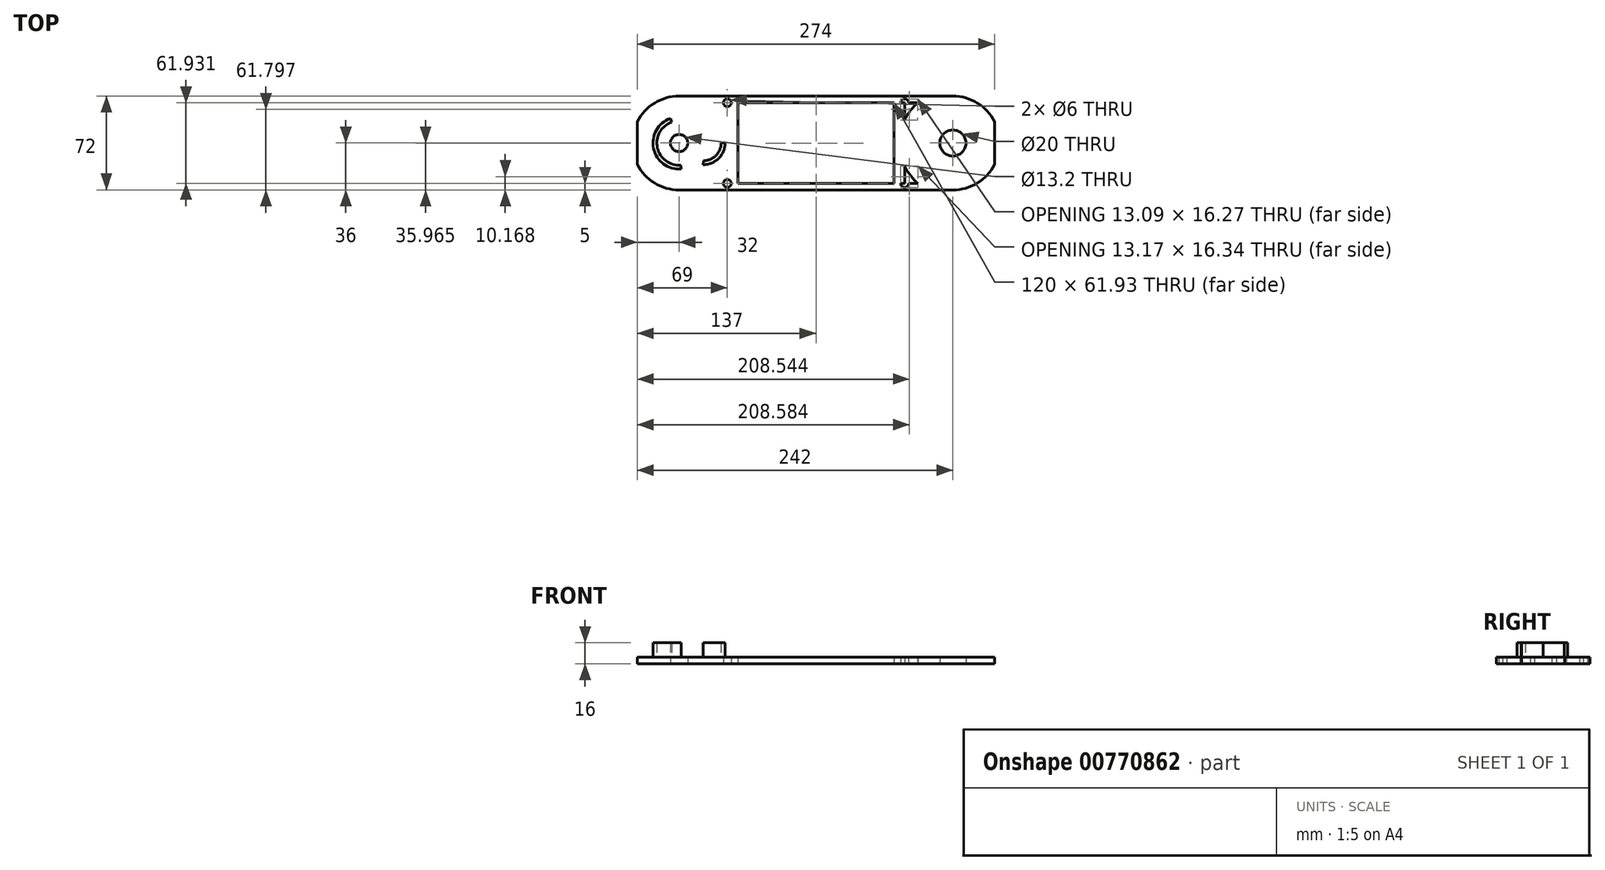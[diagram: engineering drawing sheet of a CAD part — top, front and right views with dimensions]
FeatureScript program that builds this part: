
annotation { "Feature Type Name" : "Feature", "Feature Type Description" : "" }
export const myFeature = defineFeature(function(context is Context, id is Id, definition is map)
    precondition{}
    {
        {
            var Q0;
            Q0=qCreatedBy(makeId("Top.planeOp"),FACE);
            var sketch = newSketch(context, id + "F0", { "sketchPlane" : qUnion([Q0])});
            skCircle(sketch, "E0", {"center": v(0, 0) * mm, "radius": 36 * mm});
            skCircle(sketch, "E1", {"center": v(210, 0) * mm, "radius": 36 * mm});
            skLineSegment(sketch, "E2", {"start": v(0, 36) * mm, "end": v(210, 36) * mm});
            skLineSegment(sketch, "E3", {"start": v(210, -36) * mm, "end": v(0, -36) * mm});
            skCircle(sketch, "E4", {"center": v(0, 0) * mm, "radius": 6.6 * mm});
            skCircle(sketch, "E5", {"center": v(0, 0) * mm, "radius": 10 * mm});
            skCircle(sketch, "E6", {"center": v(0, 0) * mm, "radius": 30 * mm});
            skCircle(sketch, "E7", {"center": v(210, 0) * mm, "radius": 30 * mm});
            skCircle(sketch, "E8", {"center": v(210, 0) * mm, "radius": 10 * mm});
            skCircle(sketch, "E9", {"center": v(210, 0) * mm, "radius": 14 * mm});
            skLineSegment(sketch, "E10", {"start": v(18.42, 30.93) * mm, "end": v(191.58, 30.93) * mm});
            skLineSegment(sketch, "E11", {"start": v(18.3, -31) * mm, "end": v(191.7, -31) * mm});
            skLineSegment(sketch, "E12", {"start": v(165, 30.93) * mm, "end": v(165, -31) * mm});
            skLineSegment(sketch, "E13", {"start": v(45, 30.93) * mm, "end": v(45, -31) * mm});
            skCircle(sketch, "E14", {"center": v(210, 0) * mm, "radius": 41 * mm});
            skCircle(sketch, "E15", {"center": v(0, 0) * mm, "radius": 41 * mm});
            skLineSegment(sketch, "E16.bottom", {"start": v(37, 30.93) * mm, "end": v(173, 30.93) * mm});
            skLineSegment(sketch, "E16.top", {"start": v(37, -31) * mm, "end": v(173, -31) * mm});
            skLineSegment(sketch, "E16.left", {"start": v(37, 30.93) * mm, "end": v(37, -31) * mm});
            skLineSegment(sketch, "E16.right", {"start": v(173, 30.93) * mm, "end": v(173, -31) * mm});
            skCircle(sketch, "E17", {"center": v(37, 30.93) * mm, "radius": 3 * mm});
            skCircle(sketch, "E18", {"center": v(37, -31) * mm, "radius": 3 * mm});
            skCircle(sketch, "E19", {"center": v(173, 30.93) * mm, "radius": 3 * mm});
            skCircle(sketch, "E20", {"center": v(173, -31) * mm, "radius": 3 * mm});
            skLineSegment(sketch, "E21", {"start": v(-32, -16.5) * mm, "end": v(-32, 16.5) * mm});
            skLineSegment(sketch, "E22", {"start": v(242, -16.5) * mm, "end": v(242, 16.5) * mm});
            skSolve(sketch);
        }
        {
            var Q0;
            {var subQ0=sQuery(id+"F0.wireOp",EDGE,"E16.left");var subQ1=sQuery(id+"F0.wireOp",EDGE,"E15");var subQ2=makeQuery(id+"F0.imprint","INTERSECT",VERTEX,{"disambiguationData":[OD(0.0)],"derivedFrom":[subQ1,subQ0]});Q0=makeQuery(id+"F0.imprint","IMPRINT",FACE,{"disambiguationData":[TD([[makeQuery(id+"F0.imprint","IMPRINT",EDGE,{"disambiguationData":[TD([[subQ2,1.0]])],"derivedFrom":subQ1}),1.0]])]});}
            var Q1;
            Q1=makeQuery(id+"F0.imprint","IMPRINT",FACE,{"disambiguationData":[TD([[makeQuery(id+"F0.imprint","IMPRINT",EDGE,{"derivedFrom":sQuery(id+"F0.wireOp",EDGE,"E4")}),-1.0]])]});
            var Q2;
            {var subQ0=sQuery(id+"F0.wireOp",EDGE,"E2");var subQ1=sQuery(id+"F0.wireOp",EDGE,"E1");var subQ2=makeQuery(id+"F0.imprint","INTERSECT",VERTEX,{"derivedFrom":[subQ1,subQ0]});Q2=makeQuery(id+"F0.imprint","IMPRINT",FACE,{"disambiguationData":[TD([[makeQuery(id+"F0.imprint","IMPRINT",EDGE,{"disambiguationData":[TD([[subQ2,-1.0]])],"derivedFrom":subQ1}),-1.0]])]});}
            var Q3;
            Q3=makeQuery(id+"F0.imprint","IMPRINT",FACE,{"disambiguationData":[TD([[makeQuery(id+"F0.imprint","IMPRINT",EDGE,{"derivedFrom":sQuery(id+"F0.wireOp",EDGE,"E5")}),-1.0]])]});
            var Q4;
            Q4=makeQuery(id+"F0.imprint","IMPRINT",FACE,{"disambiguationData":[TD([[makeQuery(id+"F0.imprint","IMPRINT",EDGE,{"derivedFrom":sQuery(id+"F0.wireOp",EDGE,"E8")}),-1.0]])]});
            var Q5;
            {var subQ0=sQuery(id+"F0.wireOp",EDGE,"E3");var subQ1=sQuery(id+"F0.wireOp",EDGE,"E0");var subQ2=makeQuery(id+"F0.imprint","INTERSECT",VERTEX,{"derivedFrom":[subQ1,subQ0]});Q5=makeQuery(id+"F0.imprint","IMPRINT",FACE,{"disambiguationData":[TD([[makeQuery(id+"F0.imprint","IMPRINT",EDGE,{"disambiguationData":[TD([[subQ2,-1.0]])],"derivedFrom":subQ1}),-1.0]])]});}
            var Q6;
            Q6=makeQuery(id+"F0.imprint","IMPRINT",FACE,{"disambiguationData":[TD([[makeQuery(id+"F0.imprint","IMPRINT",EDGE,{"derivedFrom":sQuery(id+"F0.wireOp",EDGE,"E7")}),-1.0]])]});
            var Q7;
            Q7=makeQuery(id+"F0.imprint","IMPRINT",FACE,{"disambiguationData":[TD([[makeQuery(id+"F0.imprint","IMPRINT",EDGE,{"derivedFrom":sQuery(id+"F0.wireOp",EDGE,"E7")}),1.0]])]});
            var Q8;
            Q8=makeQuery(id+"F0.imprint","IMPRINT",FACE,{"disambiguationData":[TD([[makeQuery(id+"F0.imprint","IMPRINT",EDGE,{"derivedFrom":sQuery(id+"F0.wireOp",EDGE,"E6")}),-1.0]])]});
            var Q9;
            {var subQ1=sQuery(id+"F0.wireOp",EDGE,"E10");var subQ5=sQuery(id+"F0.wireOp",EDGE,"E0");var subQ6=makeQuery(id+"F0.imprint","INTERSECT",VERTEX,{"derivedFrom":[subQ5,subQ1]});Q9=makeQuery(id+"F0.imprint","IMPRINT",FACE,{"disambiguationData":[TD([[makeQuery(id+"F0.imprint","IMPRINT",EDGE,{"disambiguationData":[TD([[subQ6,1.0]])],"derivedFrom":subQ5}),-1.0]])]});}
            var Q10;
            {var subQ1=sQuery(id+"F0.wireOp",EDGE,"E12");Q10=makeQuery(id+"F0.imprint","IMPRINT",FACE,{"disambiguationData":[TD([[makeQuery(id+"F0.imprint","IMPRINT",EDGE,{"derivedFrom":subQ1}),1.0]])]});}
            var Q11;
            {var subQ1=sQuery(id+"F0.wireOp",EDGE,"E1");var subQ5=sQuery(id+"F0.wireOp",EDGE,"E10");var subQ9=makeQuery(id+"F0.imprint","INTERSECT",VERTEX,{"derivedFrom":[subQ1,subQ5]});Q11=makeQuery(id+"F0.imprint","IMPRINT",FACE,{"disambiguationData":[TD([[makeQuery(id+"F0.imprint","IMPRINT",EDGE,{"disambiguationData":[TD([[subQ9,-1.0]])],"derivedFrom":subQ1}),-1.0]])]});}
            var Q12;
            {var subQ0=sQuery(id+"F0.wireOp",EDGE,"E19");var subQ1=sQuery(id+"F0.wireOp",EDGE,"E10");var subQ2=makeQuery(id+"F0.imprint","INTERSECT",VERTEX,{"derivedFrom":[subQ1,subQ0]});Q12=makeQuery(id+"F0.imprint","IMPRINT",FACE,{"disambiguationData":[TD([[makeQuery(id+"F0.imprint","IMPRINT",EDGE,{"disambiguationData":[TD([[subQ2,-1.0]])],"derivedFrom":subQ1}),-1.0]])]});}
            var Q13;
            {var subQ1=sQuery(id+"F0.wireOp",EDGE,"E13");Q13=makeQuery(id+"F0.imprint","IMPRINT",FACE,{"disambiguationData":[TD([[makeQuery(id+"F0.imprint","IMPRINT",EDGE,{"derivedFrom":subQ1}),-1.0]])]});}
            var Q14;
            {var subQ0=sQuery(id+"F0.wireOp",EDGE,"E2");var subQ1=sQuery(id+"F0.wireOp",EDGE,"E0");var subQ2=makeQuery(id+"F0.imprint","INTERSECT",VERTEX,{"derivedFrom":[subQ1,subQ0]});Q14=makeQuery(id+"F0.imprint","IMPRINT",FACE,{"disambiguationData":[TD([[makeQuery(id+"F0.imprint","IMPRINT",EDGE,{"disambiguationData":[TD([[subQ2,1.0]])],"derivedFrom":subQ1}),-1.0]])]});}
            var Q15;
            {var subQ0=sQuery(id+"F0.wireOp",EDGE,"E20");var subQ1=sQuery(id+"F0.wireOp",EDGE,"E11");var subQ2=makeQuery(id+"F0.imprint","INTERSECT",VERTEX,{"derivedFrom":[subQ1,subQ0]});Q15=makeQuery(id+"F0.imprint","IMPRINT",FACE,{"disambiguationData":[TD([[makeQuery(id+"F0.imprint","IMPRINT",EDGE,{"disambiguationData":[TD([[subQ2,-1.0]])],"derivedFrom":subQ1}),1.0]])]});}
            var Q16;
            {var subQ0=sQuery(id+"F0.wireOp",EDGE,"E15");var subQ1=sQuery(id+"F0.wireOp",EDGE,"E10");var subQ2=makeQuery(id+"F0.imprint","INTERSECT",VERTEX,{"derivedFrom":[subQ1,subQ0]});Q16=makeQuery(id+"F0.imprint","IMPRINT",FACE,{"disambiguationData":[TD([[makeQuery(id+"F0.imprint","IMPRINT",EDGE,{"disambiguationData":[TD([[subQ2,-1.0]])],"derivedFrom":subQ1}),-1.0]])]});}
            var Q17;
            {var subQ0=sQuery(id+"F0.wireOp",EDGE,"E14");var subQ1=sQuery(id+"F0.wireOp",EDGE,"E3");var subQ2=makeQuery(id+"F0.imprint","INTERSECT",VERTEX,{"derivedFrom":[subQ1,subQ0]});Q17=makeQuery(id+"F0.imprint","IMPRINT",FACE,{"disambiguationData":[TD([[makeQuery(id+"F0.imprint","IMPRINT",EDGE,{"disambiguationData":[TD([[subQ2,-1.0]])],"derivedFrom":subQ1}),-1.0]])]});}
            var Q18;
            {var subQ0=sQuery(id+"F0.wireOp",EDGE,"E15");var subQ6=sQuery(id+"F0.wireOp",EDGE,"E2");var subQ11=makeQuery(id+"F0.imprint","INTERSECT",VERTEX,{"derivedFrom":[subQ6,subQ0]});Q18=makeQuery(id+"F0.imprint","IMPRINT",FACE,{"disambiguationData":[TD([[makeQuery(id+"F0.imprint","IMPRINT",EDGE,{"disambiguationData":[TD([[subQ11,-1.0]])],"derivedFrom":subQ6}),-1.0]])]});}
            var Q19;
            {var subQ0=sQuery(id+"F0.wireOp",EDGE,"E16.right");var subQ1=sQuery(id+"F0.wireOp",EDGE,"E14");var subQ2=makeQuery(id+"F0.imprint","INTERSECT",VERTEX,{"disambiguationData":[OD(0.0)],"derivedFrom":[subQ1,subQ0]});Q19=makeQuery(id+"F0.imprint","IMPRINT",FACE,{"disambiguationData":[TD([[makeQuery(id+"F0.imprint","IMPRINT",EDGE,{"disambiguationData":[TD([[subQ2,-1.0]])],"derivedFrom":subQ1}),1.0]])]});}
            var Q20;
            {var subQ0=sQuery(id+"F0.wireOp",EDGE,"E15");var subQ1=sQuery(id+"F0.wireOp",EDGE,"E11");var subQ2=makeQuery(id+"F0.imprint","INTERSECT",VERTEX,{"derivedFrom":[subQ1,subQ0]});Q20=makeQuery(id+"F0.imprint","IMPRINT",FACE,{"disambiguationData":[TD([[makeQuery(id+"F0.imprint","IMPRINT",EDGE,{"disambiguationData":[TD([[subQ2,-1.0]])],"derivedFrom":subQ1}),1.0]])]});}
            var Q21;
            {var subQ0=sQuery(id+"F0.wireOp",EDGE,"E3");var subQ1=sQuery(id+"F0.wireOp",EDGE,"E1");var subQ2=makeQuery(id+"F0.imprint","INTERSECT",VERTEX,{"derivedFrom":[subQ1,subQ0]});Q21=makeQuery(id+"F0.imprint","IMPRINT",FACE,{"disambiguationData":[TD([[makeQuery(id+"F0.imprint","IMPRINT",EDGE,{"disambiguationData":[TD([[subQ2,1.0]])],"derivedFrom":subQ1}),-1.0]])]});}
            extrude(context, id + "F1", {"entities" : qUnion([Q0, Q1, Q2, Q3, Q4, Q5, Q6, Q7, Q8, Q9, Q10, Q11, Q12, Q13, Q14, Q15, Q16, Q17, Q18, Q19, Q20, Q21]), "depth" : 5 * mm, "offsetDistance" : 25 * mm});
        }
        {
            var Q0;
            Q0=makeQuery(id+"F1.opExtrude","CAP_FACE",FACE,{"disambiguationData":[OSD([sQuery(id+"F0.wireOp",EDGE,"E0"),sQuery(id+"F0.wireOp",EDGE,"E1"),sQuery(id+"F0.wireOp",EDGE,"E2"),sQuery(id+"F0.wireOp",EDGE,"E3"),sQuery(id+"F0.wireOp",EDGE,"E4"),sQuery(id+"F0.wireOp",EDGE,"E8"),sQuery(id+"F0.wireOp",EDGE,"E12"),sQuery(id+"F0.wireOp",EDGE,"E13"),sQuery(id+"F0.wireOp",EDGE,"E16.bottom"),sQuery(id+"F0.wireOp",EDGE,"E16.top"),sQuery(id+"F0.wireOp",EDGE,"E17"),sQuery(id+"F0.wireOp",EDGE,"E18"),sQuery(id+"F0.wireOp",EDGE,"E19"),sQuery(id+"F0.wireOp",EDGE,"E20"),sQuery(id+"F0.wireOp",EDGE,"E21"),sQuery(id+"F0.wireOp",EDGE,"E22")])],"isStart":false});
            var sketch = newSketch(context, id + "F2", { "sketchPlane" : qUnion([Q0])});
            skCircle(sketch, "E23", {"center": v(0, 0) * mm, "radius": 2.1 * mm});
            skArc(sketch, "E24", {"start": v(-5.63, 16.04) * mm, "mid": v(-16.62, -3.54) * mm, "end": v(1.4, -16.94) * mm});
            skArc(sketch, "E25.0", {"start": v(-6.63, 18.87) * mm, "mid": v(-19.55, -4.17) * mm, "end": v(1.65, -19.93) * mm});
            skLineSegment(sketch, "E26", {"start": v(-6.63, 18.87) * mm, "end": v(-5.63, 16.04) * mm});
            skLineSegment(sketch, "E27", {"start": v(1.65, -19.93) * mm, "end": v(1.4, -16.94) * mm});
            skArc(sketch, "E28", {"start": v(18.63, -13.6) * mm, "mid": v(28.25, -9.62) * mm, "end": v(32.23, 0) * mm});
            skArc(sketch, "E29.0", {"start": v(18.63, -16.6) * mm, "mid": v(30.37, -11.74) * mm, "end": v(35.23, 0) * mm});
            skLineSegment(sketch, "E30", {"start": v(18.63, -13.6) * mm, "end": v(18.63, -16.6) * mm});
            skLineSegment(sketch, "E31", {"start": v(32.23, 0) * mm, "end": v(35.23, 0) * mm});
            skSolve(sketch);
        }
        {
            var Q0;
            Q0=makeQuery(id+"F2.imprint","IMPRINT",FACE,{"disambiguationData":[TD([[makeQuery(id+"F2.imprint","IMPRINT",EDGE,{"derivedFrom":sQuery(id+"F2.wireOp",EDGE,"E28")}),-1.0]])]});
            var Q1;
            Q1=makeQuery(id+"F2.imprint","IMPRINT",FACE,{"disambiguationData":[TD([[makeQuery(id+"F2.imprint","IMPRINT",EDGE,{"derivedFrom":sQuery(id+"F2.wireOp",EDGE,"E24")}),-1.0]])]});
            extrude(context, id + "F3", {"entities" : qUnion([Q0, Q1]), "operationType" : NewBodyOperationType.ADD, "depth" : 11 * mm, "offsetDistance" : 25 * mm});
        }
    });
